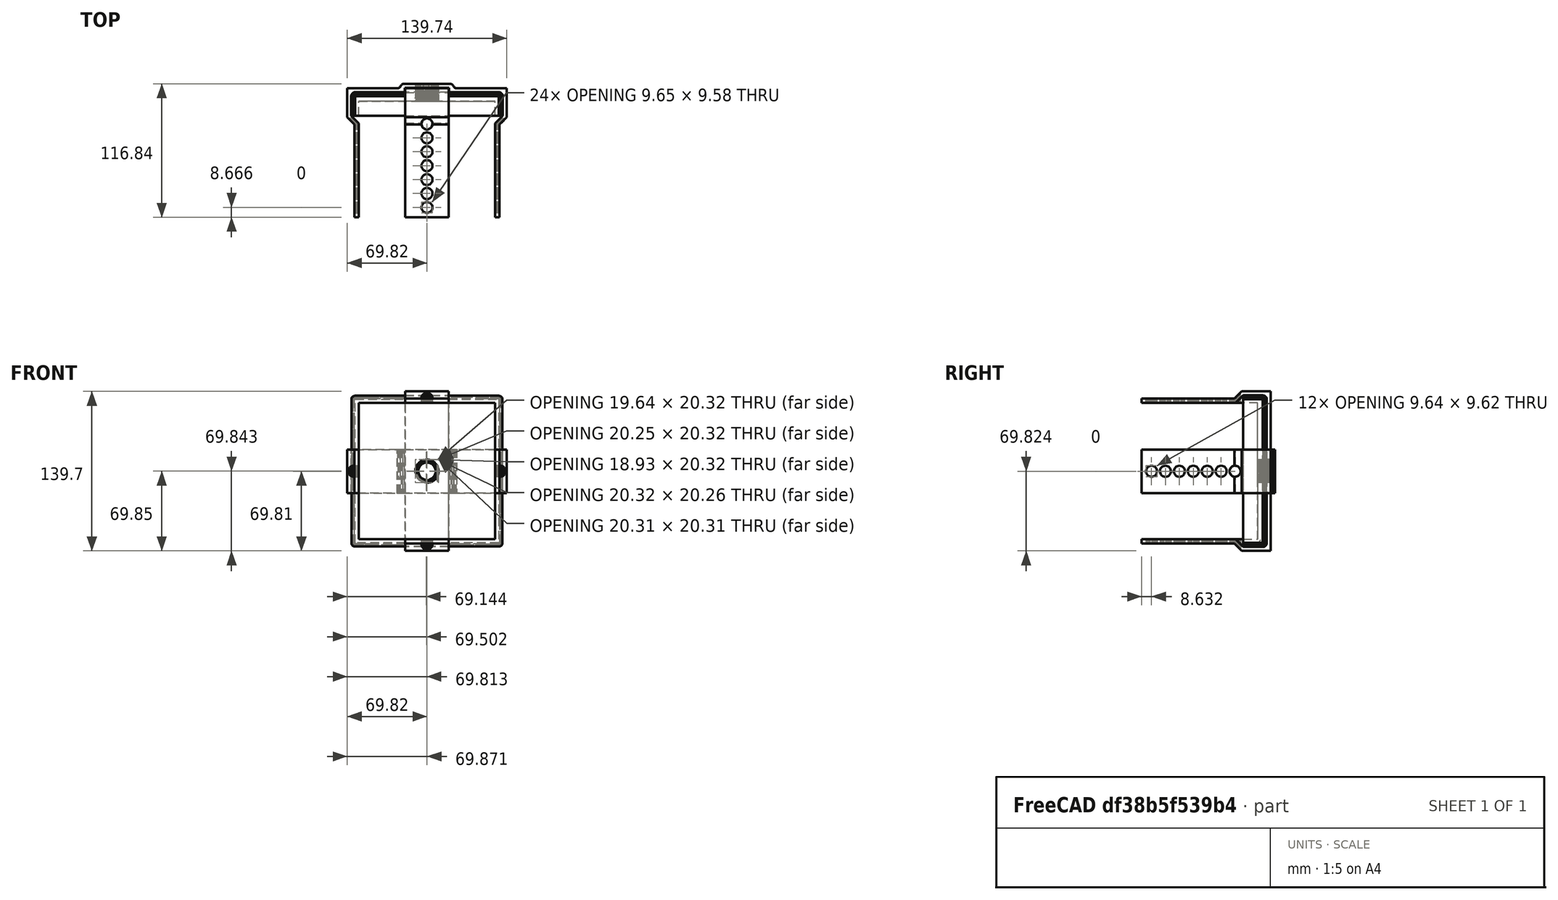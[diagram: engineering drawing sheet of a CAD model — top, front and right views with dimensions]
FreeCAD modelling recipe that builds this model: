
FCSTD DOCUMENT  (FreeCAD 1.0R39109 (Git))
Label: Edit_mm
License: All rights reserved
LicenseURL: http://en.wikipedia.org/wiki/All_rights_reserved
objects: Part::Feature×9, Part::Cut×8, PartDesign::Pad×6, Sketcher::SketchObject×5, PartDesign::Body×5, App::Part×3, Mesh::Feature×2, PartDesign::FeatureBase×1, PartDesign::Pocket×1
note: 55 computed .brp shape members not serialized (recipe doc carries the construction recipe); baked Part::Feature solids carry a one-line shape summary decoded from their .brp

FEATURE [Mesh::Feature] metric_lid  label="lid_mesh"
FEATURE [Part::Feature] metric_lid001  label="lid001"
  shape: bbox 132.1 x 113 x 139.7 mm, 2804 faces, 0 solids (baked)
FEATURE [Part::Feature] metric_lid001_solid  label="lid001 (Solid)"
  Placement = pos=(-207.189,-159.385,-12.91) rot=(0,0,1;0rad)
  shape: bbox 132.1 x 113 x 139.7 mm, 2804 faces (baked)
FEATURE [Sketcher::SketchObject] Sketch
  ArcFitTolerance = 1e-06
  AttachmentSupport = -> [YZ_Plane002]
  ExternalGeometry = -> [metric_lid001_solid]
  FullyConstrained = true
  MakeInternals = false
  MapMode = 5
  Placement = pos=(0,0,0) rot=(0.57735,0.57735,0.57735;2.0944rad)
  sketch-geometry (17):
    g0: ArcOfCircle [constr] CenterX=17.145 CenterY=122.555 CenterZ=0 NormalX=0 NormalY=0 NormalZ=1 AngleXU=0 Radius=3.17499 StartAngle=0 EndAngle=1.5708
    g1: ArcOfCircle [constr] CenterX=17.145 CenterY=-3.17501 CenterZ=0 NormalX=0 NormalY=0 NormalZ=1 AngleXU=0 Radius=3.17499 StartAngle=4.71239 EndAngle=6.28319
    g2: LineSegment [constr] StartX=-9.18115e-06 StartY=125.73 StartZ=0 EndX=17.145 EndY=125.73 EndZ=0
    g3: LineSegment [constr] StartX=17.145 StartY=-6.35 StartZ=0 EndX=-9.18115e-06 EndY=-6.35 EndZ=0
    g4: LineSegment [constr] StartX=20.32 StartY=122.555 StartZ=0 EndX=20.32 EndY=-3.175 EndZ=0
    g5: LineSegment [constr] StartX=-9.18115e-06 StartY=125.73 StartZ=0 EndX=-6.35003 EndY=119.38 EndZ=0
    g6: LineSegment [constr] StartX=-9.18115e-06 StartY=-6.35 StartZ=0 EndX=-6.35002 EndY=4e-16 EndZ=0
    g7: LineSegment [constr] StartX=-6.35003 StartY=119.38 StartZ=0 EndX=-6.35002 EndY=1.2e-15 EndZ=0
    g8: LineSegment StartX=0 StartY=126.03 StartZ=0 EndX=17.145 EndY=126.03 EndZ=0
    g9: LineSegment StartX=0 StartY=126.03 StartZ=0 EndX=-6.65001 EndY=119.38 EndZ=0
    g10: ArcOfCircle CenterX=17.145 CenterY=122.555 CenterZ=0 NormalX=0 NormalY=0 NormalZ=1 AngleXU=0 Radius=3.47499 StartAngle=0 EndAngle=1.5708
    g11: LineSegment StartX=0 StartY=-6.65 StartZ=0 EndX=-6.65001 EndY=3e-16 EndZ=0
    g12: LineSegment StartX=0 StartY=-6.65 StartZ=0 EndX=17.145 EndY=-6.65 EndZ=0
    g13: GeomPoint X=20.62 Y=-3.175 Z=0
    g14: ArcOfCircle CenterX=17.145 CenterY=-3.17501 CenterZ=0 NormalX=0 NormalY=0 NormalZ=1 AngleXU=0 Radius=3.47499 StartAngle=4.71239 EndAngle=6.28319
    g15: LineSegment StartX=-6.65001 StartY=119.38 StartZ=0 EndX=-6.65001 EndY=0 EndZ=0
    g16: LineSegment StartX=20.62 StartY=-3.175 StartZ=0 EndX=20.62 EndY=122.555 EndZ=0
  constraints (45):
    c: Coincident(g1,g-4)
    c: Vertical(g1,g1)
    c: Coincident(g0,g-4)
    c: Coincident(g0,g-6)
    c: Vertical(g0,g0)
    c: Coincident(g2,g-3)
    c: Coincident(g2,g0)
    c: Coincident(g3,g-9)
    c: Coincident(g1,g3)
    c: Coincident(g1,g-9)
    c: Coincident(g4,g0)
    c: Coincident(g4,g1)
    c: Coincident(g5,g2)
    c: PointOnObject(g5,g-8)
    c: Parallel(g5,g-11)
    c: Coincident(g6,g3)
    c: PointOnObject(g6,g-1)
    c: Parallel(g6,g-10)
    c: Coincident(g5,g7)
    c: Coincident(g6,g7)
    c: PointOnObject(g8,g-2)
    c: Horizontal(g8)
    c: Vertical(g8,g0)
    c: Coincident(g9,g8)
    c: PointOnObject(g9,g-8)
    c: Parallel(g9,g5)
    c: Coincident(g10,g0)
    c: Coincident(g10,g8)
    c: Horizontal(g10,g0)
    c: PointOnObject(g11,g-2)
    c: PointOnObject(g11,g-1)
    c: Coincident(g12,g11)
    c: Horizontal(g12)
    c: Vertical(g12,g1)
    c: Horizontal(g13,g1)
    c: Coincident(g14,g1)
    c: Coincident(g14,g12)
    c: Coincident(g14,g13)
    c: Parallel(g11,g6)
    c: Coincident(g15,g9)
    c: Coincident(g15,g11)
    c: Coincident(g16,g13)
    c: Vertical(g16)
    c: Distance(g8,g0) = 0.3
    c: Coincident(g10,g16)
FEATURE [Part::Feature] metric_lid001_solid001  label="metric_lid001 (Solid)001"
  Placement = pos=(-207.189,-159.385,-12.91) rot=(0,0,1;0rad)
  shape: bbox 132.1 x 113 x 139.7 mm, 2804 faces (baked)
FEATURE [PartDesign::Pad] Pad
  Direction = (1,0,0)
  Length = 140
  Length2 = 10
  Placement = pos=(0,0,0) rot=(1,1,1;2.0944rad)
  Profile = -> Sketch
  ReferenceAxis = -> Sketch [N_Axis]
  Refine = true
  Reversed = true
  Suppressed = false
  Type = 0
FEATURE [PartDesign::Pad] Pad001
  BaseFeature = -> Pad
  Direction = (1,0,0)
  Length = 10
  Length2 = 10
  Placement = pos=(0,0,0) rot=(1,1,1;2.0944rad)
  Profile = -> Sketch
  ReferenceAxis = -> Sketch [N_Axis]
  Refine = true
  Suppressed = false
  Type = 0
FEATURE [PartDesign::Body] Body001
  AllowCompound = false
  Group = -> [Sketch,Pad,Pad001]
  Origin = -> Origin002
  Tip = -> Pad001
FEATURE [Part::Feature] metric_lid001_solid002  label="metric_lid001 (Solid)002"
  Placement = pos=(-207.189,-159.385,-12.91) rot=(0,0,1;0rad)
  shape: bbox 132.1 x 113 x 139.7 mm, 2804 faces (baked)
FEATURE [Part::Cut] Cut
  Base = -> metric_lid001_solid001
  Refine = true
  Tool = -> Body001
FEATURE [Part::Cut] Cut001  label="Body003"
  Base = -> metric_lid001_solid002
  Refine = true
  Tool = -> Cut
FEATURE [Part::Cut] Cut002  label="metric_threaded_tie_only_"
  Base = -> metric_lid001_solid001
  Refine = true
  Tool = -> Body001
FEATURE [Sketcher::SketchObject] Sketch001
  ArcFitTolerance = 1e-06
  AttachmentSupport = -> [YZ_Plane003]
  FullyConstrained = false
  MakeInternals = false
  MapMode = 5
  Placement = pos=(0,0,0) rot=(0.57735,0.57735,0.57735;2.0944rad)
  sketch-geometry (4):
    g0: LineSegment StartX=0 StartY=136.628 StartZ=0 EndX=-35.4816 EndY=136.628 EndZ=0
    g1: LineSegment StartX=-35.4816 StartY=136.628 StartZ=0 EndX=-35.4816 EndY=-19.9564 EndZ=0
    g2: LineSegment StartX=-35.4816 StartY=-19.9564 StartZ=0 EndX=0 EndY=-19.9564 EndZ=0
    g3: LineSegment StartX=0 StartY=-19.9564 StartZ=0 EndX=0 EndY=136.628 EndZ=0
  constraints (9):
    c: Coincident(g0,g1)
    c: Coincident(g1,g2)
    c: Coincident(g2,g3)
    c: Coincident(g3,g0)
    c: Horizontal(g0)
    c: Horizontal(g2)
    c: Vertical(g1)
    c: Vertical(g3)
    c: PointOnObject(g0,g-2)
FEATURE [PartDesign::Pad] Pad002
  Direction = (1,0,0)
  Length = 115
  Length2 = 10
  Placement = pos=(0,0,0) rot=(1,1,1;2.0944rad)
  Profile = -> Sketch001
  ReferenceAxis = -> Sketch001 [N_Axis]
  Refine = true
  Reversed = true
  Suppressed = false
  Type = 0
FEATURE [PartDesign::Body] Body  label="Body002"
  AllowCompound = false
  Group = -> [Sketch001,Pad002]
  Origin = -> Origin003
  Tip = -> Pad002
FEATURE [Part::Cut] Cut003  label="metric_lid_only_"
  Base = -> Cut001
  Refine = true
  Tool = -> Body
FEATURE [App::Part] Part  label="threaded_tie_only"
  Group = -> [Cut,metric_lid001_solid002,Body001,Cut001,metric_lid001_solid001,Body,Cut002,Cut003]
  Origin = -> Origin
FEATURE [Sketcher::SketchObject] Sketch003
  ArcFitTolerance = 1e-06
  AttachmentSupport = -> [YZ_Plane006]
  FullyConstrained = false
  MakeInternals = false
  MapMode = 5
  Placement = pos=(0,0,0) rot=(0.57735,0.57735,0.57735;2.0944rad)
  sketch-geometry (4):
    g0: LineSegment StartX=0 StartY=136.628 StartZ=0 EndX=-35.4816 EndY=136.628 EndZ=0
    g1: LineSegment StartX=-35.4816 StartY=136.628 StartZ=0 EndX=-35.4816 EndY=-19.9564 EndZ=0
    g2: LineSegment StartX=-35.4816 StartY=-19.9564 StartZ=0 EndX=0 EndY=-19.9564 EndZ=0
    g3: LineSegment StartX=0 StartY=-19.9564 StartZ=0 EndX=0 EndY=136.628 EndZ=0
  constraints (9):
    c: Coincident(g0,g1)
    c: Coincident(g1,g2)
    c: Coincident(g2,g3)
    c: Coincident(g3,g0)
    c: Horizontal(g0)
    c: Horizontal(g2)
    c: Vertical(g1)
    c: Vertical(g3)
    c: PointOnObject(g0,g-2)
FEATURE [PartDesign::Pad] Pad005
  Direction = (1,0,0)
  Length = 115
  Length2 = 10
  Placement = pos=(0,0,0) rot=(1,1,1;2.0944rad)
  Profile = -> Sketch003
  ReferenceAxis = -> Sketch003 [N_Axis]
  Refine = true
  Reversed = true
  Suppressed = false
  Type = 0
FEATURE [PartDesign::Body] Body002  label="Body004"
  AllowCompound = false
  Group = -> [Sketch003,Pad005]
  Origin = -> Origin006
  Tip = -> Pad005
FEATURE [Part::Feature] metric_lid001_solid003  label="lid001 (Solid)003"
  Placement = pos=(-207.189,-159.385,-12.91) rot=(0,0,1;0rad)
  shape: bbox 132.1 x 113 x 139.7 mm, 2804 faces (baked)
FEATURE [Sketcher::SketchObject] Sketch002
  ArcFitTolerance = 1e-06
  AttachmentSupport = -> [YZ_Plane005]
  ExternalGeometry = -> [metric_lid001_solid003]
  FullyConstrained = true
  MakeInternals = false
  MapMode = 5
  Placement = pos=(0,0,0) rot=(0.57735,0.57735,0.57735;2.0944rad)
  sketch-geometry (17):
    g0: ArcOfCircle [constr] CenterX=17.145 CenterY=122.555 CenterZ=0 NormalX=0 NormalY=0 NormalZ=1 AngleXU=0 Radius=3.17499 StartAngle=5e-16 EndAngle=1.5708
    g1: ArcOfCircle [constr] CenterX=17.145 CenterY=-3.17501 CenterZ=0 NormalX=0 NormalY=0 NormalZ=1 AngleXU=0 Radius=3.17499 StartAngle=4.71239 EndAngle=6.28319
    g2: LineSegment [constr] StartX=-9.18115e-06 StartY=125.73 StartZ=0 EndX=17.145 EndY=125.73 EndZ=0
    g3: LineSegment [constr] StartX=17.145 StartY=-6.35 StartZ=0 EndX=-9.18115e-06 EndY=-6.35 EndZ=0
    g4: LineSegment [constr] StartX=20.32 StartY=122.555 StartZ=0 EndX=20.32 EndY=-3.175 EndZ=0
    g5: LineSegment [constr] StartX=-9.18115e-06 StartY=125.73 StartZ=0 EndX=-6.35003 EndY=119.38 EndZ=0
    g6: LineSegment [constr] StartX=-9.18115e-06 StartY=-6.35 StartZ=0 EndX=-6.35002 EndY=4e-16 EndZ=0
    g7: LineSegment [constr] StartX=-6.35003 StartY=119.38 StartZ=0 EndX=-6.35002 EndY=1.2e-15 EndZ=0
    g8: LineSegment StartX=0 StartY=125.73 StartZ=0 EndX=17.145 EndY=125.73 EndZ=0
    g9: LineSegment StartX=0 StartY=125.73 StartZ=0 EndX=-6.35001 EndY=119.38 EndZ=0
    g10: ArcOfCircle CenterX=17.145 CenterY=122.555 CenterZ=0 NormalX=0 NormalY=0 NormalZ=1 AngleXU=0 Radius=3.17499 StartAngle=0 EndAngle=1.5708
    g11: LineSegment StartX=0 StartY=-6.35 StartZ=0 EndX=-6.35001 EndY=4e-16 EndZ=0
    g12: LineSegment StartX=0 StartY=-6.35 StartZ=0 EndX=17.145 EndY=-6.35 EndZ=0
    g13: GeomPoint X=20.32 Y=-3.175 Z=0
    g14: ArcOfCircle CenterX=17.145 CenterY=-3.17501 CenterZ=0 NormalX=0 NormalY=0 NormalZ=1 AngleXU=0 Radius=3.17499 StartAngle=4.71239 EndAngle=6.28319
    g15: LineSegment StartX=-6.35001 StartY=119.38 StartZ=0 EndX=-6.35001 EndY=0 EndZ=0
    g16: LineSegment StartX=20.32 StartY=-3.175 StartZ=0 EndX=20.32 EndY=122.555 EndZ=0
  constraints (45):
    c: Coincident(g1,g-4)
    c: Vertical(g1,g1)
    c: Coincident(g0,g-4)
    c: Coincident(g0,g-6)
    c: Vertical(g0,g0)
    c: Coincident(g2,g-3)
    c: Coincident(g2,g0)
    c: Coincident(g3,g-9)
    c: Coincident(g1,g3)
    c: Coincident(g1,g-9)
    c: Coincident(g4,g0)
    c: Coincident(g4,g1)
    c: Coincident(g5,g2)
    c: PointOnObject(g5,g-8)
    c: Parallel(g5,g-11)
    c: Coincident(g6,g3)
    c: PointOnObject(g6,g-1)
    c: Parallel(g6,g-10)
    c: Coincident(g5,g7)
    c: Coincident(g6,g7)
    c: PointOnObject(g8,g-2)
    c: Horizontal(g8)
    c: Vertical(g8,g0)
    c: Coincident(g9,g8)
    c: PointOnObject(g9,g-8)
    c: Parallel(g9,g5)
    c: Coincident(g10,g0)
    c: Coincident(g10,g8)
    c: Horizontal(g10,g0)
    c: PointOnObject(g11,g-2)
    c: PointOnObject(g11,g-1)
    c: Coincident(g12,g11)
    c: Horizontal(g12)
    c: Vertical(g12,g1)
    c: Horizontal(g13,g1)
    c: Coincident(g14,g1)
    c: Coincident(g14,g12)
    c: Coincident(g14,g13)
    c: Parallel(g11,g6)
    c: Coincident(g15,g9)
    c: Coincident(g15,g11)
    c: Coincident(g16,g13)
    c: Vertical(g16)
    c: Distance(g8,g0) = 1e-06
    c: Coincident(g10,g16)
FEATURE [PartDesign::Pad] Pad003
  Direction = (1,0,0)
  Length = 140
  Length2 = 10
  Placement = pos=(0,0,0) rot=(1,1,1;2.0944rad)
  Profile = -> Sketch002
  ReferenceAxis = -> Sketch002 [N_Axis]
  Refine = true
  Reversed = true
  Suppressed = false
  Type = 0
FEATURE [PartDesign::Pad] Pad004
  BaseFeature = -> Pad003
  Direction = (1,0,0)
  Length = 10
  Length2 = 10
  Placement = pos=(0,0,0) rot=(1,1,1;2.0944rad)
  Profile = -> Sketch002
  ReferenceAxis = -> Sketch002 [N_Axis]
  Refine = true
  Suppressed = false
  Type = 0
FEATURE [PartDesign::Body] Body003  label="Body005"
  AllowCompound = false
  Group = -> [Sketch002,Pad003,Pad004]
  Origin = -> Origin005
  Tip = -> Pad004
FEATURE [Part::Feature] metric_lid001_solid004  label="metric_lid001 (Solid)004"
  Placement = pos=(-207.189,-159.385,-12.91) rot=(0,0,1;0rad)
  shape: bbox 132.1 x 113 x 139.7 mm, 2804 faces (baked)
FEATURE [Part::Cut] Cut004
  Base = -> metric_lid001_solid004
  Refine = true
  Tool = -> Body003
FEATURE [Part::Cut] Cut006  label="metric_threaded_tie_only001"
  Base = -> metric_lid001_solid004
  Refine = true
  Tool = -> Body003
FEATURE [Part::Feature] metric_lid001_solid005  label="metric_lid001 (Solid)005"
  Placement = pos=(-207.189,-159.385,-12.91) rot=(0,0,1;0rad)
  shape: bbox 132.1 x 113 x 139.7 mm, 2804 faces (baked)
FEATURE [Part::Cut] Cut005  label="Body006"
  Base = -> metric_lid001_solid005
  Refine = true
  Tool = -> Cut004
FEATURE [Part::Cut] Cut007  label="metric_lid_only001"
  Base = -> Cut005
  Refine = true
  Tool = -> Body002
FEATURE [App::Part] Part001  label="lid_only"
  Group = -> [Cut004,metric_lid001_solid005,Body003,Cut005,metric_lid001_solid004,Body002,Cut006,Cut007]
  Origin = -> Origin004
FEATURE [Mesh::Feature] metric_tie  label="tie_mesh"
  Placement = pos=(-167.15,54.3,21.55) rot=(0,0,-1;1.5708rad)
FEATURE [Part::Feature] metric_tie001  label="tie001"
  shape: bbox 139.7 x 116.8 x 38.1 mm, 2320 faces, 0 solids (baked)
FEATURE [Part::Feature] metric_tie001_solid  label="tie001 (Solid)"
  shape: bbox 139.7 x 116.8 x 38.1 mm, 2320 faces (baked)
FEATURE [PartDesign::FeatureBase] BaseFeature
  BaseFeature = -> metric_tie001_solid
  Suppressed = false
FEATURE [Sketcher::SketchObject] Sketch004
  ArcFitTolerance = 1e-06
  AttachmentOffset = pos=(0,0,-60) rot=(0,0,1;0rad)
  AttachmentSupport = -> [XY_Plane008]
  ExternalGeometry = -> [BaseFeature]
  FullyConstrained = true
  MakeInternals = false
  MapMode = 5
  Placement = pos=(0,0,60) rot=(0,1,0;3.14159rad)
  sketch-geometry (27):
    g0: LineSegment [constr] StartX=125.689 StartY=-0.0340225 StartZ=0 EndX=119.339 EndY=-6.38402 EndZ=0
    g1: LineSegment [constr] StartX=-6.41062 StartY=-0.0340225 StartZ=0 EndX=1.8e-15 EndY=-6.44465 EndZ=0
    g2: LineSegment StartX=0 StartY=-6.71063 StartZ=0 EndX=-6.71062 EndY=3e-16 EndZ=0
    g3: LineSegment StartX=-6.71062 StartY=3e-16 StartZ=0 EndX=-6.71062 EndY=17.119 EndZ=0
    g4: GeomPoint X=-3.23562 Y=20.594 Z=0
    g5: GeomPoint X=-3.23562 Y=17.119 Z=0
    g6: ArcOfCircle CenterX=-3.23562 CenterY=17.119 CenterZ=0 NormalX=0 NormalY=0 NormalZ=1 AngleXU=0 Radius=3.475 StartAngle=1.5708 EndAngle=3.14159
    g7: GeomPoint X=122.514 Y=20.594 Z=0
    g8: GeomPoint X=122.514 Y=17.119 Z=0
    g9: GeomPoint X=125.989 Y=17.119 Z=0
    g10: ArcOfCircle CenterX=122.514 CenterY=17.119 CenterZ=0 NormalX=0 NormalY=0 NormalZ=1 AngleXU=0 Radius=3.475 StartAngle=0 EndAngle=1.5708
    g11: GeomPoint X=40.2794 Y=20.594 Z=0
    g12: GeomPoint X=40.2794 Y=24.404 Z=0
    g13: GeomPoint X=78.9986 Y=24.404 Z=0
    g14: GeomPoint X=78.9986 Y=20.594 Z=0
    g15: LineSegment StartX=40.2794 StartY=24.404 StartZ=0 EndX=78.9986 EndY=24.404 EndZ=0
    g16: LineSegment StartX=78.9986 StartY=24.404 StartZ=0 EndX=78.9986 EndY=20.594 EndZ=0
    g17: LineSegment StartX=40.2794 StartY=24.404 StartZ=0 EndX=40.2794 EndY=20.594 EndZ=0
    g18: LineSegment StartX=-3.23562 StartY=20.594 StartZ=0 EndX=40.2794 EndY=20.594 EndZ=0
    g19: LineSegment [constr] StartX=40.5794 StartY=20.294 StartZ=0 EndX=40.2794 EndY=20.594 EndZ=0
    g20: LineSegment [constr] StartX=40.5794 StartY=24.104 StartZ=0 EndX=40.2794 EndY=24.404 EndZ=0
    g21: LineSegment [constr] StartX=78.6986 StartY=20.294 StartZ=0 EndX=78.9986 EndY=20.594 EndZ=0
    g22: LineSegment [constr] StartX=78.6986 StartY=24.104 StartZ=0 EndX=78.9986 EndY=24.404 EndZ=0
    g23: LineSegment StartX=78.9986 StartY=20.594 StartZ=0 EndX=122.514 EndY=20.594 EndZ=0
    g24: LineSegment StartX=125.989 StartY=17.119 StartZ=0 EndX=125.989 EndY=0 EndZ=0
    g25: LineSegment StartX=125.989 StartY=0 StartZ=0 EndX=119.339 EndY=-6.65001 EndZ=0
    g26: LineSegment StartX=0 StartY=-6.71063 StartZ=0 EndX=119.339 EndY=-6.65001 EndZ=0
  constraints (61):
    c: Coincident(g0,g-5)
    c: PointOnObject(g0,g-4)
    c: Parallel(g0,g-9)
    c: Coincident(g1,g-3)
    c: PointOnObject(g1,g-2)
    c: Parallel(g1,g-8)
    c: PointOnObject(g2,g-2)
    c: PointOnObject(g2,g-1)
    c: Coincident(g3,g2)
    c: Vertical(g3)
    c: Horizontal(g3,g-3)
    c: Vertical(g4,g-6)
    c: Horizontal(g5,g-3)
    c: Vertical(g5,g-6)
    c: Coincident(g6,g5)
    c: Coincident(g6,g3)
    c: Coincident(g6,g4)
    c: Distance(g3,g-3) = 0.3  'dddd'
    c: Parallel(g2,g1)
    c: Vertical(g7,g-7)
    c: Vertical(g8,g-7)
    c: Horizontal(g8,g-5)
    c: Horizontal(g9,g-5)
    c: Coincident(g10,g8)
    c: Coincident(g10,g7)
    c: Coincident(g10,g9)
    c: Horizontal(g11,g4)
    c: Vertical(g12,g11)
    c: Horizontal(g13,g12)
    c: Vertical(g14,g13)
    c: Coincident(g15,g12)
    c: Coincident(g15,g13)
    c: Coincident(g16,g13)
    c: Coincident(g16,g14)
    c: Coincident(g17,g12)
    c: Coincident(g17,g11)
    c: Coincident(g18,g4)
    c: Coincident(g18,g11)
    c: Coincident(g19,g-6)
    c: Coincident(g19,g11)
    c: Angle(g19,g-6) = 0.785398
    c: Coincident(g20,g-10)
    c: Coincident(g20,g12)
    c: Parallel(g20,g19)
    c: Coincident(g21,g-7)
    c: Coincident(g21,g14)
    c: Coincident(g22,g-10)
    c: Coincident(g22,g13)
    c: Parallel(g21,g22)
    c: Angle(g-7,g21) = 0.785398
    c: Coincident(g23,g14)
    c: Coincident(g23,g7)
    c: Horizontal(g23)
    c: Coincident(g24,g9)
    c: PointOnObject(g24,g-1)
    c: Vertical(g24)
    c: Coincident(g25,g24)
    c: PointOnObject(g25,g-4)
    c: Parallel(g25,g0)
    c: Coincident(g25,g26)
    c: Coincident(g2,g26)
FEATURE [PartDesign::Pocket] Pocket
  BaseFeature = -> BaseFeature
  Direction = (0,0,1)
  Length = 100
  Length2 = 5
  Midplane = true
  Profile = -> Sketch004
  ReferenceAxis = -> Sketch004 [N_Axis]
  Refine = true
  Suppressed = false
  Type = 0
FEATURE [PartDesign::Body] Body004  label="Body"
  AllowCompound = false
  BaseFeature = -> metric_tie001_solid
  Group = -> [BaseFeature,Sketch004,Pocket]
  Origin = -> Origin008
  Tip = -> Pocket
FEATURE [App::Part] Part002  label="tie"
  Group = -> [Body004]
  Origin = -> Origin007
